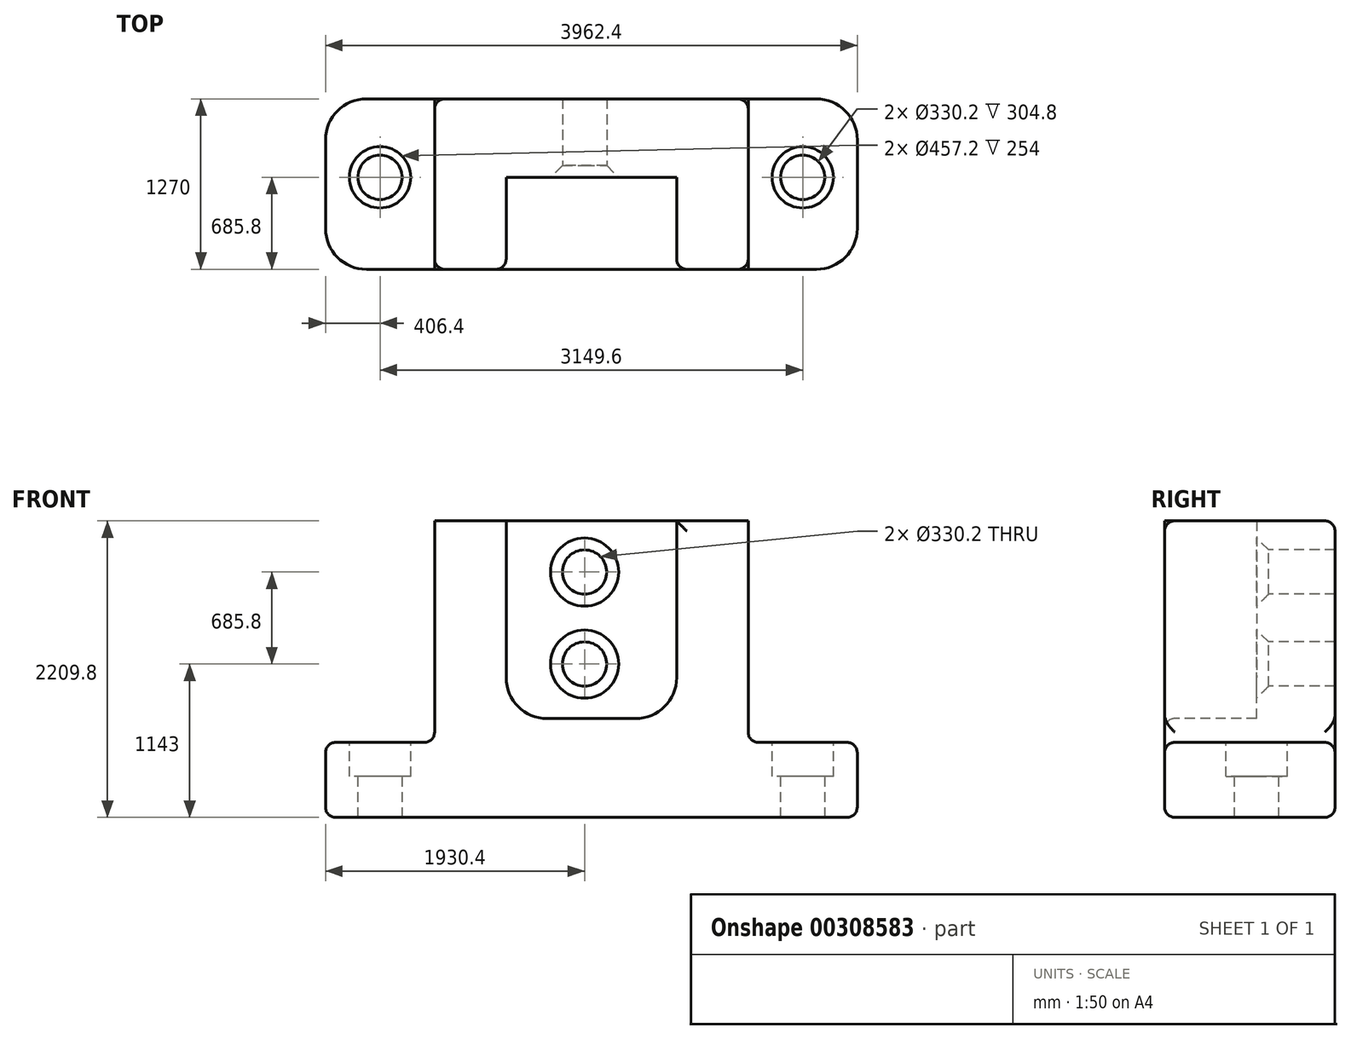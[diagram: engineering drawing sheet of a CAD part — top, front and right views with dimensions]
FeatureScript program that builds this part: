
annotation { "Feature Type Name" : "Feature", "Feature Type Description" : "" }
export const myFeature = defineFeature(function(context is Context, id is Id, definition is map)
    precondition{}
    {
        {
            var Q0;
            Q0=qCreatedBy(makeId("Front.planeOp"),FACE);
            var sketch = newSketch(context, id + "F0", { "sketchPlane" : qUnion([Q0])});
            skLineSegment(sketch, "E0.bottom", {"start": v(-1996.77, 1058.34) * mm, "end": v(1965.63, 1058.34) * mm});
            skLineSegment(sketch, "E0.top", {"start": v(-1996.77, -1151.46) * mm, "end": v(1965.63, -1151.46) * mm});
            skLineSegment(sketch, "E0.left", {"start": v(-1996.77, 1058.34) * mm, "end": v(-1996.77, -1151.46) * mm});
            skLineSegment(sketch, "E0.right", {"start": v(1965.63, 1058.34) * mm, "end": v(1965.63, -1151.46) * mm});
            skSolve(sketch);
        }
        {
            var Q0;
            Q0=makeQuery(id+"F0.imprint","IMPRINT",FACE,{"disambiguationData":[TD([[makeQuery(id+"F0.imprint","IMPRINT",EDGE,{"derivedFrom":sQuery(id+"F0.wireOp",EDGE,"E0.bottom")}),-1.0]])]});
            extrude(context, id + "F1", {"entities" : qUnion([Q0]), "depth" : 1270 * mm});
        }
        {
            var Q0;
            Q0=makeQuery(id+"F1.opExtrude","CAP_FACE",FACE,{"disambiguationData":[OSD([sQuery(id+"F0.wireOp",EDGE,"E0.bottom"),sQuery(id+"F0.wireOp",EDGE,"E0.top"),sQuery(id+"F0.wireOp",EDGE,"E0.left"),sQuery(id+"F0.wireOp",EDGE,"E0.right")])],"isStart":false});
            var sketch = newSketch(context, id + "F2", { "sketchPlane" : qUnion([Q0])});
            skLineSegment(sketch, "E1", {"start": v(1152.83, 1058.34) * mm, "end": v(1152.83, -592.66) * mm});
            skLineSegment(sketch, "E2", {"start": v(1152.83, -592.66) * mm, "end": v(1965.63, -592.66) * mm});
            skLineSegment(sketch, "E3", {"start": v(-1183.97, 1058.34) * mm, "end": v(-1183.97, -592.66) * mm});
            skLineSegment(sketch, "E4", {"start": v(-1183.97, -592.66) * mm, "end": v(-1996.77, -592.66) * mm});
            skSolve(sketch);
        }
        {
            var Q0;
            {var subQ0=sQuery(id+"F2.wireOp",EDGE,"E3");Q0=makeQuery(id+"F2.imprint","IMPRINT",FACE,{"disambiguationData":[TD([[makeQuery(id+"F2.imprint","IMPRINT",EDGE,{"derivedFrom":subQ0}),-1.0]])]});}
            var Q1;
            {var subQ0=sQuery(id+"F2.wireOp",EDGE,"E1");Q1=makeQuery(id+"F2.imprint","IMPRINT",FACE,{"disambiguationData":[TD([[makeQuery(id+"F2.imprint","IMPRINT",EDGE,{"derivedFrom":subQ0}),1.0]])]});}
            extrude(context, id + "F3", {"entities" : qUnion([Q0, Q1]), "operationType" : NewBodyOperationType.REMOVE, "oppositeDirection" : true, "depth" : 1270 * mm});
        }
        {
            var Q0;
            Q0=makeQuery(id+"F1.opExtrude","CAP_FACE",FACE,{"disambiguationData":[OSD([sQuery(id+"F0.wireOp",EDGE,"E0.bottom"),sQuery(id+"F0.wireOp",EDGE,"E0.top"),sQuery(id+"F0.wireOp",EDGE,"E0.left"),sQuery(id+"F0.wireOp",EDGE,"E0.right")])],"isStart":false});
            var sketch = newSketch(context, id + "F4", { "sketchPlane" : qUnion([Q0])});
            skLineSegment(sketch, "E5", {"start": v(-650.57, 1058.34) * mm, "end": v(-650.57, -414.86) * mm});
            skLineSegment(sketch, "E6", {"start": v(-650.57, -414.86) * mm, "end": v(619.43, -414.86) * mm});
            skLineSegment(sketch, "E7", {"start": v(619.43, -414.86) * mm, "end": v(619.43, 1058.34) * mm});
            skLineSegment(sketch, "E8", {"start": v(-1183.97, 1058.34) * mm, "end": v(-650.57, 1058.34) * mm});
            skLineSegment(sketch, "E9", {"start": v(619.43, 1058.34) * mm, "end": v(1152.83, 1058.34) * mm});
            skSolve(sketch);
        }
        {
            var Q0;
            {var subQ0=sQuery(id+"F4.wireOp",EDGE,"E5");Q0=makeQuery(id+"F4.imprint","IMPRINT",FACE,{"disambiguationData":[TD([[makeQuery(id+"F4.imprint","IMPRINT",EDGE,{"derivedFrom":subQ0}),1.0]])]});}
            extrude(context, id + "F5", {"entities" : qUnion([Q0]), "operationType" : NewBodyOperationType.REMOVE, "oppositeDirection" : true, "depth" : 685.8 * mm});
        }
        {
            var Q0;
            Q0=makeQuery(id+"F3.boolean.opBoolean","COPY",FACE,{"derivedFrom":makeQuery(id+"F3.opExtrude","SWEPT_FACE",FACE,{"disambiguationData":[OSD([sQuery(id+"F2.wireOp",EDGE,"E2")])]})});
            var sketch = newSketch(context, id + "F6", { "sketchPlane" : qUnion([Q0])});
            skLineSegment(sketch, "E10", {"start": v(1559.23, 0) * mm, "end": v(1559.23, -584.2) * mm});
            skLineSegment(sketch, "E11", {"start": v(1559.23, -584.2) * mm, "end": v(1965.63, -584.2) * mm});
            skSolve(sketch);
        }
        {
            var Q0;
            Q0=sQuery(id+"F6.wireOp",VERTEX,"E11.start");
            var Q1;
            Q1=makeQuery(id+"F1.opExtrude","SWEPT_BODY",BODY,{"disambiguationData":[OSD([sQuery(id+"F0.wireOp",EDGE,"E0.bottom"),sQuery(id+"F0.wireOp",EDGE,"E0.top"),sQuery(id+"F0.wireOp",EDGE,"E0.left"),sQuery(id+"F0.wireOp",EDGE,"E0.right")])]});
            hole(context, id + "F7", {"style" : HoleStyle.C_BORE, "endStyle" : HoleEndStyle.THROUGH, "holeDiameter" : 330.2 * mm, "cBoreDiameter" : 457.2 * mm, "cBoreDepth" : 254 * mm, "tappedDepth" : 12.7 * mm, "tapClearance" : 3, "locations" : qUnion([Q0]), "scope" : qUnion([Q1])});
        }
        {
            var Q0;
            Q0=makeQuery(id+"F3.boolean.opBoolean","COPY",FACE,{"derivedFrom":makeQuery(id+"F3.opExtrude","SWEPT_FACE",FACE,{"disambiguationData":[OSD([sQuery(id+"F2.wireOp",EDGE,"E4")])]})});
            var sketch = newSketch(context, id + "F8", { "sketchPlane" : qUnion([Q0])});
            skLineSegment(sketch, "E12", {"start": v(-1590.37, 0) * mm, "end": v(-1590.37, -584.2) * mm});
            skLineSegment(sketch, "E13", {"start": v(-1590.37, -584.2) * mm, "end": v(-1996.77, -584.2) * mm});
            skSolve(sketch);
        }
        {
            var Q0;
            Q0=sQuery(id+"F8.wireOp",VERTEX,"E13.start");
            var Q1;
            Q1=makeQuery(id+"F1.opExtrude","SWEPT_BODY",BODY,{"disambiguationData":[OSD([sQuery(id+"F0.wireOp",EDGE,"E0.bottom"),sQuery(id+"F0.wireOp",EDGE,"E0.top"),sQuery(id+"F0.wireOp",EDGE,"E0.left"),sQuery(id+"F0.wireOp",EDGE,"E0.right")])]});
            hole(context, id + "F9", {"style" : HoleStyle.C_BORE, "endStyle" : HoleEndStyle.THROUGH, "holeDiameter" : 330.2 * mm, "cBoreDiameter" : 457.2 * mm, "cBoreDepth" : 254 * mm, "tappedDepth" : 12.7 * mm, "tapClearance" : 3, "locations" : qUnion([Q0]), "scope" : qUnion([Q1])});
        }
        {
            var Q0;
            Q0=makeQuery(id+"F5.boolean.opBoolean","COPY",FACE,{"derivedFrom":makeQuery(id+"F5.opExtrude","CAP_FACE",FACE,{"disambiguationData":[OSD([sQuery(id+"F0.wireOp",EDGE,"E0.bottom"),sQuery(id+"F4.wireOp",EDGE,"E5"),sQuery(id+"F4.wireOp",EDGE,"E6"),sQuery(id+"F4.wireOp",EDGE,"E7")])],"isStart":false})});
            var sketch = newSketch(context, id + "F10", { "sketchPlane" : qUnion([Q0])});
            skLineSegment(sketch, "E14", {"start": v(-66.37, 1058.34) * mm, "end": v(-66.37, 677.34) * mm});
            skLineSegment(sketch, "E15", {"start": v(-66.37, 677.34) * mm, "end": v(-650.57, 677.34) * mm});
            skLineSegment(sketch, "E16", {"start": v(-66.37, 1058.34) * mm, "end": v(-66.37, -8.46) * mm});
            skLineSegment(sketch, "E17", {"start": v(-66.37, -8.46) * mm, "end": v(-650.57, -8.46) * mm});
            skSolve(sketch);
        }
        {
            var Q0;
            Q0=sQuery(id+"F10.wireOp",VERTEX,"E15.start");
            var Q1;
            Q1=sQuery(id+"F10.wireOp",VERTEX,"E16.end");
            var Q2;
            Q2=makeQuery(id+"F1.opExtrude","SWEPT_BODY",BODY,{"disambiguationData":[OSD([sQuery(id+"F0.wireOp",EDGE,"E0.bottom"),sQuery(id+"F0.wireOp",EDGE,"E0.top"),sQuery(id+"F0.wireOp",EDGE,"E0.left"),sQuery(id+"F0.wireOp",EDGE,"E0.right")])]});
            hole(context, id + "F11", {"style" : HoleStyle.C_SINK, "endStyle" : HoleEndStyle.THROUGH, "holeDiameter" : 330.2 * mm, "cSinkDiameter" : 508 * mm, "cSinkAngle" : 90 * degree, "tappedDepth" : 12.7 * mm, "tapClearance" : 3, "locations" : qUnion([Q0, Q1]), "scope" : qUnion([Q2])});
        }
        {
            var Q0;
            Q0=makeQuery(id+"F1.opExtrude","CAP_EDGE",EDGE,{"disambiguationData":[OSD([sQuery(id+"F0.wireOp",EDGE,"E0.left")])],"isStart":false});
            var Q1;
            Q1=makeQuery(id+"F1.opExtrude","CAP_EDGE",EDGE,{"disambiguationData":[OSD([sQuery(id+"F0.wireOp",EDGE,"E0.right")])],"isStart":false});
            var Q2;
            Q2=makeQuery(id+"F1.opExtrude","CAP_EDGE",EDGE,{"disambiguationData":[OSD([sQuery(id+"F0.wireOp",EDGE,"E0.right")])],"isStart":true});
            var Q3;
            Q3=makeQuery(id+"F5.boolean.opBoolean","COPY",EDGE,{"derivedFrom":makeQuery(id+"F5.opExtrude","SWEPT_EDGE",EDGE,{"disambiguationData":[OSD([sQuery(id+"F4.wireOp",EDGE,"E5"),sQuery(id+"F4.wireOp",EDGE,"E6")])]})});
            var Q4;
            Q4=makeQuery(id+"F5.boolean.opBoolean","COPY",EDGE,{"derivedFrom":makeQuery(id+"F5.opExtrude","SWEPT_EDGE",EDGE,{"disambiguationData":[OSD([sQuery(id+"F4.wireOp",EDGE,"E6"),sQuery(id+"F4.wireOp",EDGE,"E7")])]})});
            var Q5;
            Q5=makeQuery(id+"F1.opExtrude","CAP_EDGE",EDGE,{"disambiguationData":[OSD([sQuery(id+"F0.wireOp",EDGE,"E0.left")])],"isStart":true});
            fillet(context, id + "F12", {"entities" : qUnion([Q0, Q1, Q2, Q3, Q4, Q5]), "radius" : 304.8 * mm, "tangentPropagation" : true, "allowEdgeOverflow" : false});
        }
        {
            var Q0;
            Q0=makeQuery(id+"F3.boolean.opBoolean","COPY",EDGE,{"derivedFrom":makeQuery(id+"F3.opExtrude","SWEPT_EDGE",EDGE,{"disambiguationData":[OSD([sQuery(id+"F0.wireOp",EDGE,"E0.bottom"),sQuery(id+"F2.wireOp",EDGE,"E3")])]})});
            var Q1;
            Q1=makeQuery(id+"F1.opExtrude","CAP_EDGE",EDGE,{"disambiguationData":[OSD([sQuery(id+"F0.wireOp",EDGE,"E0.bottom")])],"isStart":true});
            var Q2;
            Q2=makeQuery(id+"F5.boolean.opBoolean","COPY",EDGE,{"derivedFrom":makeQuery(id+"F5.opExtrude","CAP_EDGE",EDGE,{"disambiguationData":[OSD([sQuery(id+"F0.wireOp",EDGE,"E0.bottom")])],"isStart":false})});
            var Q3;
            Q3=makeQuery(id+"F5.boolean.opBoolean","COPY",EDGE,{"derivedFrom":makeQuery(id+"F5.opExtrude","SWEPT_EDGE",EDGE,{"disambiguationData":[OSD([sQuery(id+"F0.wireOp",EDGE,"E0.bottom"),sQuery(id+"F4.wireOp",EDGE,"E7"),sQuery(id+"F4.wireOp",EDGE,"E9")])]})});
            var Q4;
            Q4=makeQuery(id+"F5.boolean.opBoolean","COPY",EDGE,{"derivedFrom":makeQuery(id+"F5.opExtrude","SWEPT_EDGE",EDGE,{"disambiguationData":[OSD([sQuery(id+"F0.wireOp",EDGE,"E0.bottom"),sQuery(id+"F4.wireOp",EDGE,"E5"),sQuery(id+"F4.wireOp",EDGE,"E8")])]})});
            var Q5;
            {var subQ0=sQuery(id+"F0.wireOp",EDGE,"E0.bottom");Q5=makeQuery(id+"F5.boolean.opBoolean","SPLIT",EDGE,{"disambiguationData":[TD([makeQuery(id+"F3.boolean.opBoolean","COPY",FACE,{"derivedFrom":makeQuery(id+"F3.opExtrude","SWEPT_FACE",FACE,{"disambiguationData":[OSD([sQuery(id+"F2.wireOp",EDGE,"E1")])]})})])],"derivedFrom":makeQuery(id+"F1.opExtrude","CAP_EDGE",EDGE,{"disambiguationData":[OSD([subQ0])],"isStart":false})});}
            var Q6;
            Q6=makeQuery(id+"F3.boolean.opBoolean","COPY",EDGE,{"derivedFrom":makeQuery(id+"F3.opExtrude","SWEPT_EDGE",EDGE,{"disambiguationData":[OSD([sQuery(id+"F0.wireOp",EDGE,"E0.bottom"),sQuery(id+"F2.wireOp",EDGE,"E1")])]})});
            var Q7;
            Q7=makeQuery(id+"F3.boolean.opBoolean","COPY",EDGE,{"derivedFrom":makeQuery(id+"F3.opExtrude","SWEPT_EDGE",EDGE,{"disambiguationData":[OSD([sQuery(id+"F0.wireOp",EDGE,"E0.left"),sQuery(id+"F2.wireOp",EDGE,"E4")])]})});
            var Q8;
            Q8=makeQuery(id+"F12.opFillet","BLEND_EDGE",EDGE,{"blendedFrom":[makeQuery(id+"F1.opExtrude","CAP_EDGE",EDGE,{"disambiguationData":[OSD([sQuery(id+"F0.wireOp",EDGE,"E0.left")])],"isStart":true}),makeQuery(id+"F3.boolean.opBoolean","COPY",FACE,{"derivedFrom":makeQuery(id+"F3.opExtrude","SWEPT_FACE",FACE,{"disambiguationData":[OSD([sQuery(id+"F2.wireOp",EDGE,"E4")])]})})],"blendedInto":[makeQuery(id+"F3.boolean.opBoolean","COPY",FACE,{"derivedFrom":makeQuery(id+"F3.opExtrude","SWEPT_FACE",FACE,{"disambiguationData":[OSD([sQuery(id+"F2.wireOp",EDGE,"E4")])]})})]});
            var Q9;
            Q9=makeQuery(id+"F3.boolean.opBoolean","COPY",EDGE,{"derivedFrom":makeQuery(id+"F3.opExtrude","CAP_EDGE",EDGE,{"disambiguationData":[OSD([sQuery(id+"F2.wireOp",EDGE,"E4")])],"isStart":false})});
            var Q10;
            Q10=makeQuery(id+"F12.opFillet","BLEND_EDGE",EDGE,{"blendedFrom":[makeQuery(id+"F1.opExtrude","CAP_EDGE",EDGE,{"disambiguationData":[OSD([sQuery(id+"F0.wireOp",EDGE,"E0.left")])],"isStart":false}),makeQuery(id+"F3.boolean.opBoolean","COPY",FACE,{"derivedFrom":makeQuery(id+"F3.opExtrude","SWEPT_FACE",FACE,{"disambiguationData":[OSD([sQuery(id+"F2.wireOp",EDGE,"E4")])]})})],"blendedInto":[makeQuery(id+"F3.boolean.opBoolean","COPY",FACE,{"derivedFrom":makeQuery(id+"F3.opExtrude","SWEPT_FACE",FACE,{"disambiguationData":[OSD([sQuery(id+"F2.wireOp",EDGE,"E4")])]})})]});
            var Q11;
            Q11=makeQuery(id+"F3.boolean.opBoolean","COPY",EDGE,{"derivedFrom":makeQuery(id+"F3.opExtrude","CAP_EDGE",EDGE,{"disambiguationData":[OSD([sQuery(id+"F2.wireOp",EDGE,"E4")])],"isStart":true})});
            var Q12;
            Q12=makeQuery(id+"F3.boolean.opBoolean","COPY",EDGE,{"derivedFrom":makeQuery(id+"F3.opExtrude","SWEPT_EDGE",EDGE,{"disambiguationData":[OSD([sQuery(id+"F2.wireOp",EDGE,"E3"),sQuery(id+"F2.wireOp",EDGE,"E4")])]})});
            var Q13;
            Q13=makeQuery(id+"F1.opExtrude","CAP_EDGE",EDGE,{"disambiguationData":[OSD([sQuery(id+"F0.wireOp",EDGE,"E0.top")])],"isStart":false});
            var Q14;
            Q14=makeQuery(id+"F12.opFillet","BLEND_EDGE",EDGE,{"blendedFrom":[makeQuery(id+"F1.opExtrude","CAP_EDGE",EDGE,{"disambiguationData":[OSD([sQuery(id+"F0.wireOp",EDGE,"E0.left")])],"isStart":false}),makeQuery(id+"F1.opExtrude","SWEPT_FACE",FACE,{"disambiguationData":[OSD([sQuery(id+"F0.wireOp",EDGE,"E0.top")])]})],"blendedInto":[makeQuery(id+"F1.opExtrude","SWEPT_FACE",FACE,{"disambiguationData":[OSD([sQuery(id+"F0.wireOp",EDGE,"E0.top")])]})]});
            var Q15;
            Q15=makeQuery(id+"F1.opExtrude","SWEPT_EDGE",EDGE,{"disambiguationData":[OSD([sQuery(id+"F0.wireOp",EDGE,"E0.top"),sQuery(id+"F0.wireOp",EDGE,"E0.left")])]});
            var Q16;
            Q16=makeQuery(id+"F12.opFillet","BLEND_EDGE",EDGE,{"blendedFrom":[makeQuery(id+"F1.opExtrude","CAP_EDGE",EDGE,{"disambiguationData":[OSD([sQuery(id+"F0.wireOp",EDGE,"E0.left")])],"isStart":true}),makeQuery(id+"F1.opExtrude","SWEPT_FACE",FACE,{"disambiguationData":[OSD([sQuery(id+"F0.wireOp",EDGE,"E0.top")])]})],"blendedInto":[makeQuery(id+"F1.opExtrude","SWEPT_FACE",FACE,{"disambiguationData":[OSD([sQuery(id+"F0.wireOp",EDGE,"E0.top")])]})]});
            var Q17;
            Q17=makeQuery(id+"F5.boolean.opBoolean","COPY",EDGE,{"derivedFrom":makeQuery(id+"F5.opExtrude","CAP_EDGE",EDGE,{"disambiguationData":[OSD([sQuery(id+"F4.wireOp",EDGE,"E7")])],"isStart":true})});
            var Q18;
            Q18=makeQuery(id+"F12.opFillet","BLEND_EDGE",EDGE,{"blendedFrom":[makeQuery(id+"F5.boolean.opBoolean","COPY",EDGE,{"derivedFrom":makeQuery(id+"F5.opExtrude","SWEPT_EDGE",EDGE,{"disambiguationData":[OSD([sQuery(id+"F4.wireOp",EDGE,"E6"),sQuery(id+"F4.wireOp",EDGE,"E7")])]})}),makeQuery(id+"F1.opExtrude","CAP_FACE",FACE,{"disambiguationData":[OSD([sQuery(id+"F0.wireOp",EDGE,"E0.bottom"),sQuery(id+"F0.wireOp",EDGE,"E0.top"),sQuery(id+"F0.wireOp",EDGE,"E0.left"),sQuery(id+"F0.wireOp",EDGE,"E0.right")])],"isStart":false})],"blendedInto":[makeQuery(id+"F1.opExtrude","CAP_FACE",FACE,{"disambiguationData":[OSD([sQuery(id+"F0.wireOp",EDGE,"E0.bottom"),sQuery(id+"F0.wireOp",EDGE,"E0.top"),sQuery(id+"F0.wireOp",EDGE,"E0.left"),sQuery(id+"F0.wireOp",EDGE,"E0.right")])],"isStart":false})]});
            var Q19;
            Q19=makeQuery(id+"F5.boolean.opBoolean","COPY",EDGE,{"derivedFrom":makeQuery(id+"F5.opExtrude","CAP_EDGE",EDGE,{"disambiguationData":[OSD([sQuery(id+"F4.wireOp",EDGE,"E6")])],"isStart":true})});
            var Q20;
            Q20=makeQuery(id+"F12.opFillet","BLEND_EDGE",EDGE,{"blendedFrom":[makeQuery(id+"F5.boolean.opBoolean","COPY",EDGE,{"derivedFrom":makeQuery(id+"F5.opExtrude","SWEPT_EDGE",EDGE,{"disambiguationData":[OSD([sQuery(id+"F4.wireOp",EDGE,"E5"),sQuery(id+"F4.wireOp",EDGE,"E6")])]})}),makeQuery(id+"F1.opExtrude","CAP_FACE",FACE,{"disambiguationData":[OSD([sQuery(id+"F0.wireOp",EDGE,"E0.bottom"),sQuery(id+"F0.wireOp",EDGE,"E0.top"),sQuery(id+"F0.wireOp",EDGE,"E0.left"),sQuery(id+"F0.wireOp",EDGE,"E0.right")])],"isStart":false})],"blendedInto":[makeQuery(id+"F1.opExtrude","CAP_FACE",FACE,{"disambiguationData":[OSD([sQuery(id+"F0.wireOp",EDGE,"E0.bottom"),sQuery(id+"F0.wireOp",EDGE,"E0.top"),sQuery(id+"F0.wireOp",EDGE,"E0.left"),sQuery(id+"F0.wireOp",EDGE,"E0.right")])],"isStart":false})]});
            var Q21;
            Q21=makeQuery(id+"F5.boolean.opBoolean","COPY",EDGE,{"derivedFrom":makeQuery(id+"F5.opExtrude","CAP_EDGE",EDGE,{"disambiguationData":[OSD([sQuery(id+"F4.wireOp",EDGE,"E5")])],"isStart":true})});
            var Q22;
            Q22=makeQuery(id+"F3.boolean.opBoolean","COPY",EDGE,{"derivedFrom":makeQuery(id+"F3.opExtrude","CAP_EDGE",EDGE,{"disambiguationData":[OSD([sQuery(id+"F2.wireOp",EDGE,"E1")])],"isStart":true})});
            var Q23;
            Q23=makeQuery(id+"F3.boolean.opBoolean","COPY",EDGE,{"derivedFrom":makeQuery(id+"F3.opExtrude","CAP_EDGE",EDGE,{"disambiguationData":[OSD([sQuery(id+"F2.wireOp",EDGE,"E3")])],"isStart":true})});
            var Q24;
            Q24=makeQuery(id+"F3.boolean.opBoolean","COPY",EDGE,{"derivedFrom":makeQuery(id+"F3.opExtrude","CAP_EDGE",EDGE,{"disambiguationData":[OSD([sQuery(id+"F2.wireOp",EDGE,"E3")])],"isStart":false})});
            var Q25;
            Q25=makeQuery(id+"F3.boolean.opBoolean","COPY",EDGE,{"derivedFrom":makeQuery(id+"F3.opExtrude","CAP_EDGE",EDGE,{"disambiguationData":[OSD([sQuery(id+"F2.wireOp",EDGE,"E2")])],"isStart":true})});
            var Q26;
            Q26=makeQuery(id+"F12.opFillet","BLEND_EDGE",EDGE,{"blendedFrom":[makeQuery(id+"F1.opExtrude","CAP_EDGE",EDGE,{"disambiguationData":[OSD([sQuery(id+"F0.wireOp",EDGE,"E0.right")])],"isStart":false}),makeQuery(id+"F3.boolean.opBoolean","COPY",FACE,{"derivedFrom":makeQuery(id+"F3.opExtrude","SWEPT_FACE",FACE,{"disambiguationData":[OSD([sQuery(id+"F2.wireOp",EDGE,"E2")])]})})],"blendedInto":[makeQuery(id+"F3.boolean.opBoolean","COPY",FACE,{"derivedFrom":makeQuery(id+"F3.opExtrude","SWEPT_FACE",FACE,{"disambiguationData":[OSD([sQuery(id+"F2.wireOp",EDGE,"E2")])]})})]});
            var Q27;
            Q27=makeQuery(id+"F3.boolean.opBoolean","COPY",EDGE,{"derivedFrom":makeQuery(id+"F3.opExtrude","SWEPT_EDGE",EDGE,{"disambiguationData":[OSD([sQuery(id+"F0.wireOp",EDGE,"E0.right"),sQuery(id+"F2.wireOp",EDGE,"E2")])]})});
            var Q28;
            Q28=makeQuery(id+"F3.boolean.opBoolean","COPY",EDGE,{"derivedFrom":makeQuery(id+"F3.opExtrude","SWEPT_EDGE",EDGE,{"disambiguationData":[OSD([sQuery(id+"F2.wireOp",EDGE,"E1"),sQuery(id+"F2.wireOp",EDGE,"E2")])]})});
            var Q29;
            Q29=makeQuery(id+"F3.boolean.opBoolean","COPY",EDGE,{"derivedFrom":makeQuery(id+"F3.opExtrude","CAP_EDGE",EDGE,{"disambiguationData":[OSD([sQuery(id+"F2.wireOp",EDGE,"E1")])],"isStart":false})});
            var Q30;
            Q30=makeQuery(id+"F3.boolean.opBoolean","COPY",EDGE,{"derivedFrom":makeQuery(id+"F3.opExtrude","CAP_EDGE",EDGE,{"disambiguationData":[OSD([sQuery(id+"F2.wireOp",EDGE,"E2")])],"isStart":false})});
            var Q31;
            Q31=makeQuery(id+"F12.opFillet","BLEND_EDGE",EDGE,{"blendedFrom":[makeQuery(id+"F1.opExtrude","CAP_EDGE",EDGE,{"disambiguationData":[OSD([sQuery(id+"F0.wireOp",EDGE,"E0.right")])],"isStart":true}),makeQuery(id+"F3.boolean.opBoolean","COPY",FACE,{"derivedFrom":makeQuery(id+"F3.opExtrude","SWEPT_FACE",FACE,{"disambiguationData":[OSD([sQuery(id+"F2.wireOp",EDGE,"E2")])]})})],"blendedInto":[makeQuery(id+"F3.boolean.opBoolean","COPY",FACE,{"derivedFrom":makeQuery(id+"F3.opExtrude","SWEPT_FACE",FACE,{"disambiguationData":[OSD([sQuery(id+"F2.wireOp",EDGE,"E2")])]})})]});
            var Q32;
            Q32=makeQuery(id+"F1.opExtrude","SWEPT_EDGE",EDGE,{"disambiguationData":[OSD([sQuery(id+"F0.wireOp",EDGE,"E0.top"),sQuery(id+"F0.wireOp",EDGE,"E0.right")])]});
            var Q33;
            Q33=makeQuery(id+"F12.opFillet","BLEND_EDGE",EDGE,{"blendedFrom":[makeQuery(id+"F1.opExtrude","CAP_EDGE",EDGE,{"disambiguationData":[OSD([sQuery(id+"F0.wireOp",EDGE,"E0.right")])],"isStart":false}),makeQuery(id+"F1.opExtrude","SWEPT_FACE",FACE,{"disambiguationData":[OSD([sQuery(id+"F0.wireOp",EDGE,"E0.top")])]})],"blendedInto":[makeQuery(id+"F1.opExtrude","SWEPT_FACE",FACE,{"disambiguationData":[OSD([sQuery(id+"F0.wireOp",EDGE,"E0.top")])]})]});
            var Q34;
            Q34=makeQuery(id+"F12.opFillet","BLEND_EDGE",EDGE,{"blendedFrom":[makeQuery(id+"F1.opExtrude","CAP_EDGE",EDGE,{"disambiguationData":[OSD([sQuery(id+"F0.wireOp",EDGE,"E0.right")])],"isStart":true}),makeQuery(id+"F1.opExtrude","SWEPT_FACE",FACE,{"disambiguationData":[OSD([sQuery(id+"F0.wireOp",EDGE,"E0.top")])]})],"blendedInto":[makeQuery(id+"F1.opExtrude","SWEPT_FACE",FACE,{"disambiguationData":[OSD([sQuery(id+"F0.wireOp",EDGE,"E0.top")])]})]});
            var Q35;
            Q35=makeQuery(id+"F1.opExtrude","CAP_EDGE",EDGE,{"disambiguationData":[OSD([sQuery(id+"F0.wireOp",EDGE,"E0.top")])],"isStart":true});
            fillet(context, id + "F13", {"entities" : qUnion([Q0, Q1, Q2, Q3, Q4, Q5, Q6, Q7, Q8, Q9, Q10, Q11, Q12, Q13, Q14, Q15, Q16, Q17, Q18, Q19, Q20, Q21, Q22, Q23, Q24, Q25, Q26, Q27, Q28, Q29, Q30, Q31, Q32, Q33, Q34, Q35]), "radius" : 76.2 * mm, "tangentPropagation" : true, "allowEdgeOverflow" : false});
        }
    });
